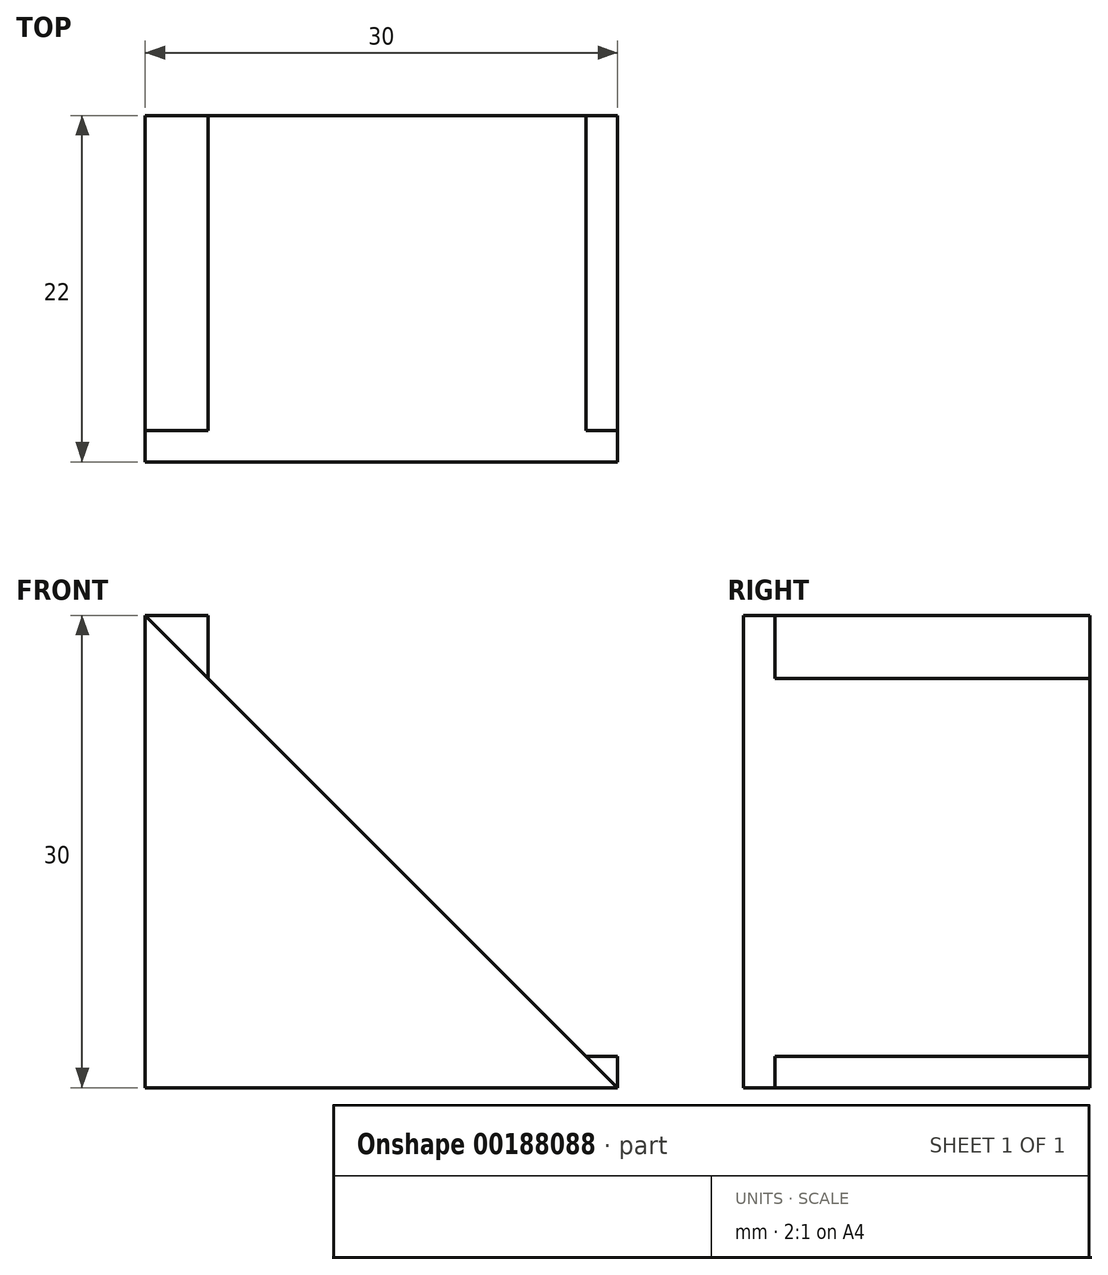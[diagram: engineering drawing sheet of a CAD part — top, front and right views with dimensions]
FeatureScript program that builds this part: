
annotation { "Feature Type Name" : "Feature", "Feature Type Description" : "" }
export const myFeature = defineFeature(function(context is Context, id is Id, definition is map)
    precondition{}
    {
        {
            var Q0;
            Q0=qCreatedBy(makeId("Front.planeOp"),FACE);
            var sketch = newSketch(context, id + "F0", { "sketchPlane" : qUnion([Q0])});
            skLineSegment(sketch, "E0", {"start": v(0, 0) * mm, "end": v(30, 0) * mm});
            skLineSegment(sketch, "E1", {"start": v(0, 0) * mm, "end": v(0, 30) * mm});
            skLineSegment(sketch, "E2", {"start": v(0, 30) * mm, "end": v(30, 0) * mm});
            skSolve(sketch);
        }
        {
            var Q0;
            Q0=qCreatedBy(makeId("Right.planeOp"),FACE);
            var sketch = newSketch(context, id + "F1", { "sketchPlane" : qUnion([Q0])});
            skLineSegment(sketch, "E3", {"start": v(0, 0) * mm, "end": v(20, 0) * mm});
            skLineSegment(sketch, "E4", {"start": v(20, 0) * mm, "end": v(20, 30) * mm});
            skLineSegment(sketch, "E5", {"start": v(20, 30) * mm, "end": v(0, 30) * mm});
            skLineSegment(sketch, "E6", {"start": v(0, 30) * mm, "end": v(0, 0) * mm});
            skSolve(sketch);
        }
        {
            var Q0;
            Q0=makeQuery(id+"F1.imprint","IMPRINT",FACE,{"disambiguationData":[TD([[makeQuery(id+"F1.imprint","IMPRINT",EDGE,{"derivedFrom":sQuery(id+"F1.wireOp",EDGE,"E3")}),1.0]])]});
            extrude(context, id + "F2", {"entities" : qUnion([Q0]), "depth" : 4 * mm});
        }
        {
            var Q0;
            Q0=qCreatedBy(makeId("Front.planeOp"),FACE);
            var sketch = newSketch(context, id + "F3", { "sketchPlane" : qUnion([Q0])});
            skLineSegment(sketch, "E7", {"start": v(0, 0) * mm, "end": v(30, 0) * mm});
            skLineSegment(sketch, "E8", {"start": v(0, 0) * mm, "end": v(0, 30) * mm});
            skLineSegment(sketch, "E9", {"start": v(0, 30) * mm, "end": v(30, 0) * mm});
            skSolve(sketch);
        }
        {
            var Q0;
            Q0=makeQuery(id+"F0.imprint","IMPRINT",FACE,{"disambiguationData":[TD([[makeQuery(id+"F0.imprint","IMPRINT",EDGE,{"derivedFrom":sQuery(id+"F0.wireOp",EDGE,"E0")}),1.0]])]});
            extrude(context, id + "F4", {"entities" : qUnion([Q0]), "operationType" : NewBodyOperationType.ADD, "depth" : 2 * mm});
        }
        {
            var Q0;
            Q0=sQuery(id+"F3.wireOp",EDGE,"E7");
            extrude(context, id + "F5", {"bodyType" : ToolBodyType.SURFACE, "surfaceEntities" : qUnion([Q0]), "oppositeDirection" : true, "depth" : 20 * mm});
        }
        {
            var Q0;
            Q0=makeQuery(id+"F5.opExtrude","SWEPT_FACE",FACE,{"disambiguationData":[OSD([sQuery(id+"F3.wireOp",EDGE,"E7")])]});
            extrude(context, id + "F6", {"entities" : qUnion([Q0]), "operationType" : NewBodyOperationType.ADD, "depth" : 2 * mm});
        }
        {
            var Q0;
            Q0=makeQuery(id+"F4.opExtrude","CAP_FACE",FACE,{"disambiguationData":[OSD([sQuery(id+"F0.wireOp",EDGE,"E0"),sQuery(id+"F0.wireOp",EDGE,"E1"),sQuery(id+"F0.wireOp",EDGE,"E2")])],"isStart":true});
            extrude(context, id + "F7", {"entities" : qUnion([Q0]), "operationType" : NewBodyOperationType.ADD, "depth" : 20 * mm});
        }
    });
